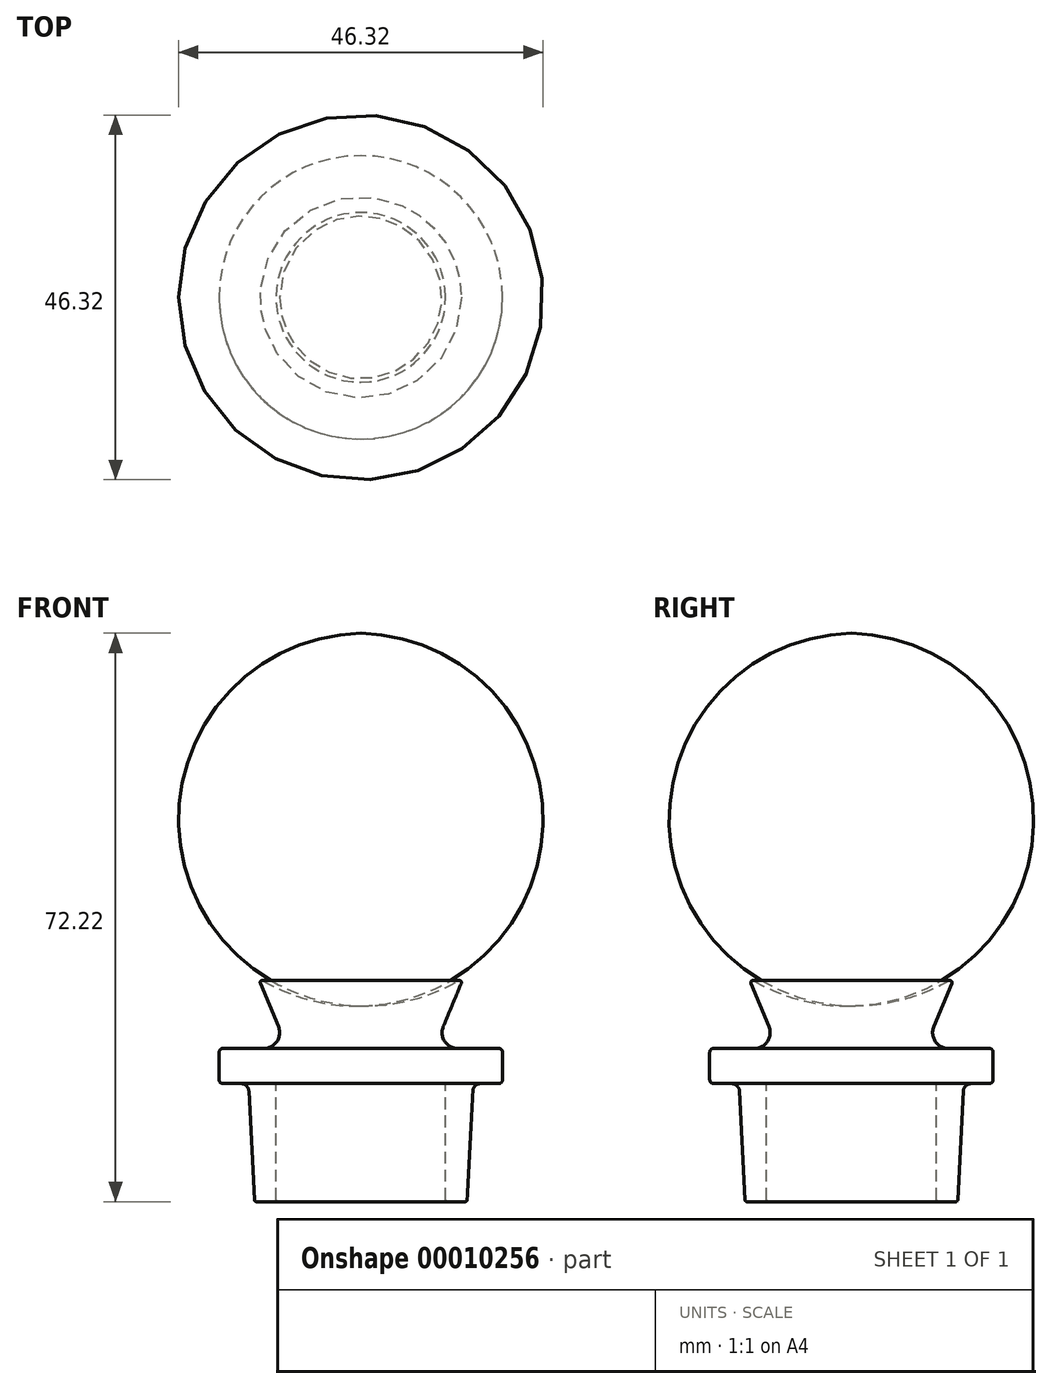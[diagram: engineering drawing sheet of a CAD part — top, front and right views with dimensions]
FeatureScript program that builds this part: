
annotation { "Feature Type Name" : "Feature", "Feature Type Description" : "" }
export const myFeature = defineFeature(function(context is Context, id is Id, definition is map)
    precondition{}
    {
        {
            var Q0;
            Q0=qCreatedBy(makeId("Front.planeOp"),FACE);
            var sketch = newSketch(context, id + "F0", { "sketchPlane" : qUnion([Q0])});
            skLineSegment(sketch, "E0", {"start": v(13.5, 0) * mm, "end": v(14.27, 15) * mm});
            skLineSegment(sketch, "E1", {"start": v(14.5, 19.47) * mm, "end": v(9.32, 19.47) * mm});
            skLineSegment(sketch, "E2", {"start": v(9.32, 19.47) * mm, "end": v(13.06, 28.45) * mm});
            skLineSegment(sketch, "E3", {"start": v(0, 24.87) * mm, "end": v(0, 15) * mm});
            skLineSegment(sketch, "E4", {"start": v(10.77, 0) * mm, "end": v(13.5, 0) * mm});
            skLineSegment(sketch, "E5", {"start": v(14.27, 15) * mm, "end": v(18, 15) * mm});
            skLineSegment(sketch, "E6", {"start": v(18, 15) * mm, "end": v(18, 19.47) * mm});
            skLineSegment(sketch, "E7", {"start": v(18, 19.47) * mm, "end": v(14.5, 19.47) * mm});
            skArc(sketch, "E8", {"start": v(0, 24.87) * mm, "mid": v(6.8, 25.7) * mm, "end": v(13.06, 28.45) * mm});
            skLineSegment(sketch, "E9", {"start": v(0, 15) * mm, "end": v(10.77, 15) * mm});
            skLineSegment(sketch, "E10", {"start": v(10.77, 15) * mm, "end": v(10.77, 0) * mm});
            skLineSegment(sketch, "E11", {"start": v(0, 15) * mm, "end": v(0, 15) * mm});
            skSolve(sketch);
        }
        {
            var Q0;
            Q0=makeQuery(id+"F0.imprint","IMPRINT",FACE,{"disambiguationData":[TD([[makeQuery(id+"F0.imprint","IMPRINT",EDGE,{"derivedFrom":sQuery(id+"F0.wireOp",EDGE,"E0")}),1.0]])]});
            var Q1;
            Q1=sQuery(id+"F0.wireOp",EDGE,"E3");
            revolve(context, id + "F1", {"entities" : qUnion([Q0]), "axis" : qUnion([Q1]), "revolveType" : RevolveType.FULL});
        }
        {
            var Q0;
            Q0=makeQuery(id+"F1.opRevolve","SWEPT_EDGE",EDGE,{"disambiguationData":[OSD([sQuery(id+"F0.wireOp",EDGE,"E1"),sQuery(id+"F0.wireOp",EDGE,"E2")])]});
            fillet(context, id + "F2", {"entities" : qUnion([Q0]), "radius" : 2 * mm, "tangentPropagation" : true, "allowEdgeOverflow" : false});
        }
        {
            var Q0;
            Q0=makeQuery(id+"F1.opRevolve","SWEPT_EDGE",EDGE,{"disambiguationData":[OSD([sQuery(id+"F0.wireOp",EDGE,"E2"),sQuery(id+"F0.wireOp",EDGE,"E8")])]});
            fillet(context, id + "F3", {"entities" : qUnion([Q0]), "radius" : 0.25 * mm, "tangentPropagation" : true, "allowEdgeOverflow" : false});
        }
        {
            var Q0;
            Q0=makeQuery(id+"F1.opRevolve","SWEPT_EDGE",EDGE,{"disambiguationData":[OSD([sQuery(id+"F0.wireOp",EDGE,"E0"),sQuery(id+"F0.wireOp",EDGE,"E5")])]});
            fillet(context, id + "F4", {"entities" : qUnion([Q0]), "radius" : 1 * mm, "tangentPropagation" : true, "allowEdgeOverflow" : false});
        }
        {
            var Q0;
            Q0=makeQuery(id+"F1.opRevolve","SWEPT_FACE",FACE,{"disambiguationData":[OSD([sQuery(id+"F0.wireOp",EDGE,"E4")])]});
            fillet(context, id + "F5", {"entities" : qUnion([Q0]), "radius" : 0.25 * mm, "tangentPropagation" : true, "allowEdgeOverflow" : false});
        }
        {
            var Q0;
            Q0=makeQuery(id+"F1.opRevolve","SWEPT_FACE",FACE,{"disambiguationData":[OSD([sQuery(id+"F0.wireOp",EDGE,"E6")])]});
            fillet(context, id + "F6", {"entities" : qUnion([Q0]), "radius" : 0.5 * mm, "tangentPropagation" : true, "allowEdgeOverflow" : false});
        }
    });
